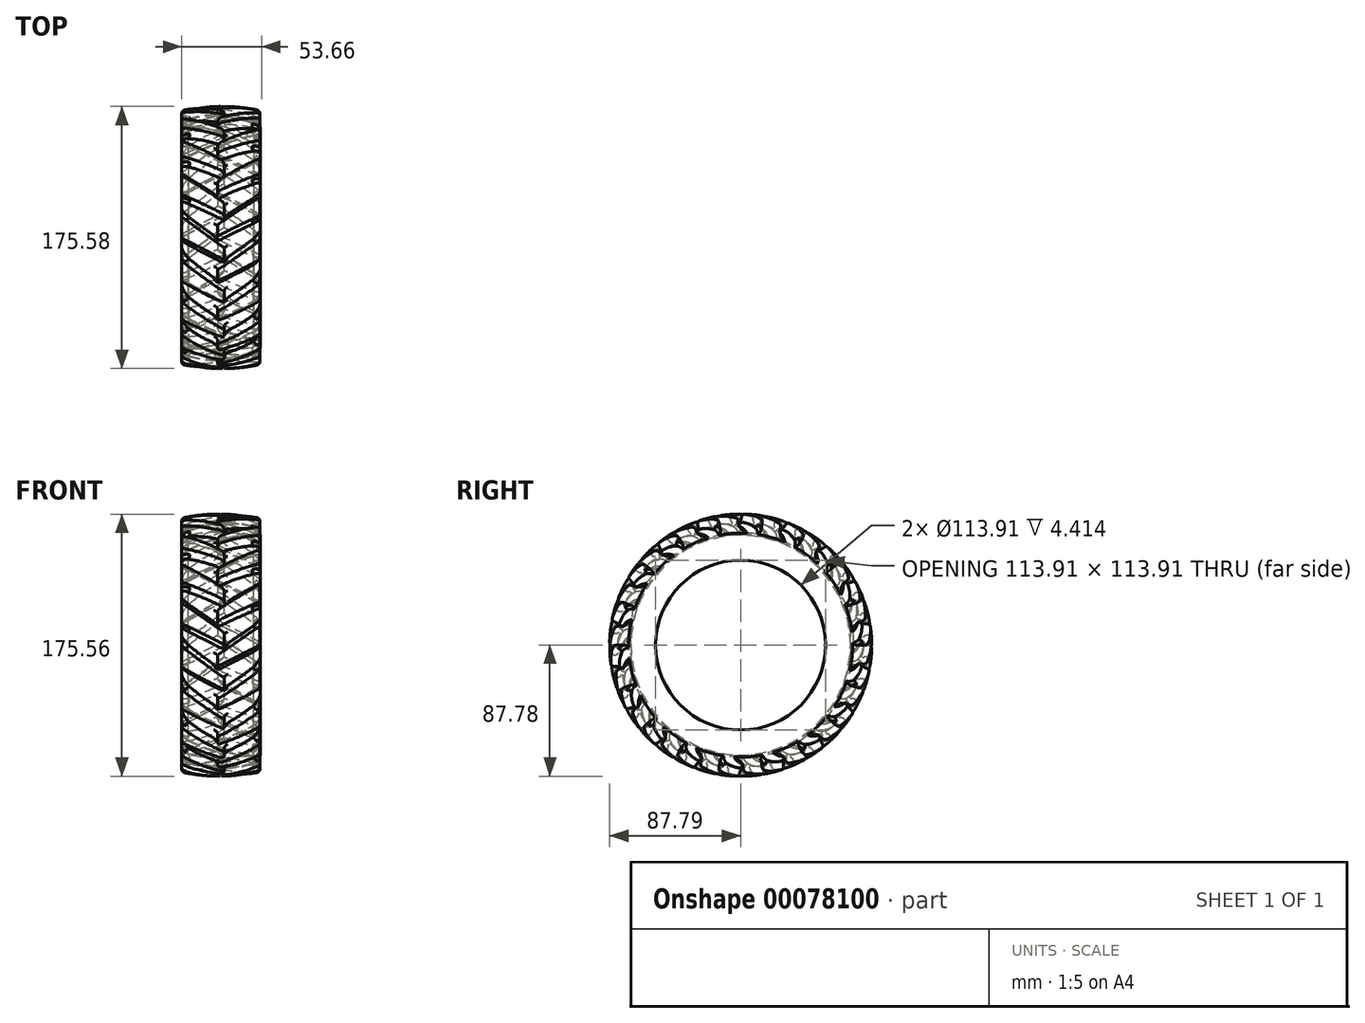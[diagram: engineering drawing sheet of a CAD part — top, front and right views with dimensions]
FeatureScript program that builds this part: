
annotation { "Feature Type Name" : "Feature", "Feature Type Description" : "" }
export const myFeature = defineFeature(function(context is Context, id is Id, definition is map)
    precondition{}
    {
        {
            var Q0;
            Q0=qCreatedBy(makeId("Top.planeOp"),FACE);
            var sketch = newSketch(context, id + "F0", { "sketchPlane" : qUnion([Q0])});
            skLineSegment(sketch, "E0", {"start": v(-41.36, 0) * mm, "end": v(39.08, 0) * mm});
            skLineSegment(sketch, "E1", {"start": v(0, 0) * mm, "end": v(0, 69.17) * mm});
            skLineSegment(sketch, "E2.bottom", {"start": v(26.28, 56.34) * mm, "end": v(-26.28, 56.34) * mm});
            skLineSegment(sketch, "E2.left", {"start": v(26.28, 56.34) * mm, "end": v(26.28, 73.43) * mm});
            skLineSegment(sketch, "E2.right", {"start": v(-26.28, 56.34) * mm, "end": v(-26.28, 73.43) * mm});
            skPoint(sketch, "E2.middle", {"position": v(0, 69.17) * mm});
            skArc(sketch, "E3", {"start": v(-21.6, 79.56) * mm, "mid": v(0, 82.44) * mm, "end": v(21.6, 79.56) * mm});
            skPoint(sketch, "E4.orphan", {"position": v(-26.28, 82) * mm});
            skPoint(sketch, "E5.orphan", {"position": v(26.28, 82) * mm});
            skPoint(sketch, "E6.visualSharp", {"position": v(-26.28, 78.14) * mm});
            skArc(sketch, "E6.filletArc", {"start": v(-21.6, 79.56) * mm, "mid": v(-24.97, 77.3) * mm, "end": v(-26.28, 73.43) * mm});
            skPoint(sketch, "E7.visualSharp", {"position": v(26.28, 78.14) * mm});
            skArc(sketch, "E7.filletArc", {"start": v(26.28, 73.43) * mm, "mid": v(24.97, 77.3) * mm, "end": v(21.6, 79.56) * mm});
            skSolve(sketch);
        }
        {
            var Q0;
            Q0 = qSketchRegion(id + "F0", true);
            var Q1;
            Q1=sQuery(id+"F0.wireOp",EDGE,"E0");
            revolve(context, id + "F1", {"entities" : qUnion([Q0]), "axis" : qUnion([Q1]), "revolveType" : RevolveType.FULL});
        }
        {
            var Q0;
            Q0=qCreatedBy(makeId("Top.planeOp"),FACE);
            var sketch = newSketch(context, id + "F2", { "sketchPlane" : qUnion([Q0])});
            skLineSegment(sketch, "E8", {"start": v(-26.25, 13.83) * mm, "end": v(2.16, -6.94) * mm});
            skLineSegment(sketch, "E9", {"start": v(2.16, -6.94) * mm, "end": v(2.16, -14.96) * mm});
            skLineSegment(sketch, "E10", {"start": v(2.16, -14.96) * mm, "end": v(-26.25, -0.3) * mm});
            skLineSegment(sketch, "E11", {"start": v(-26.25, 13.83) * mm, "end": v(-26.25, 0) * mm});
            skLineSegment(sketch, "E12", {"start": v(-26.25, 0) * mm, "end": v(-26.25, -0.3) * mm});
            skPoint(sketch, "E13.orphan", {"position": v(-26.83, 0) * mm});
            skLineSegment(sketch, "E14", {"start": v(-49.96, 0) * mm, "end": v(51.5, 0) * mm});
            skSolve(sketch);
        }
        {
            var Q0;
            Q0=makeQuery(id+"F2.imprint","IMPRINT",FACE,{"disambiguationData":[TD([[makeQuery(id+"F2.imprint","IMPRINT",EDGE,{"derivedFrom":sQuery(id+"F2.wireOp",EDGE,"E8")}),-1.0]])]});
            var Q1;
            {var subQ1=sQuery(id+"F2.wireOp",EDGE,"E9");Q1=makeQuery(id+"F2.imprint","IMPRINT",FACE,{"disambiguationData":[TD([[makeQuery(id+"F2.imprint","IMPRINT",EDGE,{"derivedFrom":subQ1}),-1.0]])]});}
            extrude(context, id + "F3", {"entities" : qUnion([Q0, Q1]), "operationType" : NewBodyOperationType.ADD, "depth" : 88.9 * mm});
        }
        {
            var Q0;
            Q0=qCreatedBy(makeId("Top.planeOp"),FACE);
            var Q1;
            Q1=sQuery(id+"F2.wireOp",EDGE,"E14");
            cPlane(context, id + "F4", {"entities" : qUnion([Q0, Q1]), "cplaneType" : CPlaneType.LINE_ANGLE, "offset" : 152.4 * mm, "angle" : 10 * degree, "width" : 152.4 * mm, "height" : 152.4 * mm});
        }
        {
            var Q0;
            Q0=qCreatedBy(id+"F4.planeOp",FACE);
            var sketch = newSketch(context, id + "F5", { "sketchPlane" : qUnion([Q0])});
            skLineSegment(sketch, "E15", {"start": v(-2.2, 14.33) * mm, "end": v(-2.2, 6.63) * mm});
            skLineSegment(sketch, "E16", {"start": v(-2.2, 6.63) * mm, "end": v(26.07, -12.68) * mm});
            skLineSegment(sketch, "E17", {"start": v(26.07, -12.68) * mm, "end": v(26.07, 0) * mm});
            skLineSegment(sketch, "E18", {"start": v(26.07, 0) * mm, "end": v(-2.2, 14.33) * mm});
            skSolve(sketch);
        }
        {
            var Q0;
            Q0=makeQuery(id+"F5.imprint","IMPRINT",FACE,{"disambiguationData":[TD([[makeQuery(id+"F5.imprint","IMPRINT",EDGE,{"derivedFrom":sQuery(id+"F5.wireOp",EDGE,"E15")}),1.0]])]});
            extrude(context, id + "F6", {"entities" : qUnion([Q0]), "operationType" : NewBodyOperationType.ADD, "oppositeDirection" : true, "depth" : 88.9 * mm});
        }
        {
            var Q0;
            Q0=qCreatedBy(makeId("Front.planeOp"),FACE);
            var sketch = newSketch(context, id + "F7", { "sketchPlane" : qUnion([Q0])});
            skArc(sketch, "E19", {"start": v(33.67, -83.2) * mm, "mid": v(-0.3, -87.8) * mm, "end": v(-34.27, -83.04) * mm});
            skLineSegment(sketch, "E20", {"start": v(-34.27, -83.04) * mm, "end": v(-34.27, -99.42) * mm});
            skLineSegment(sketch, "E21", {"start": v(-34.27, -99.42) * mm, "end": v(37.55, -99.42) * mm});
            skLineSegment(sketch, "E22", {"start": v(37.55, -99.42) * mm, "end": v(33.67, -83.2) * mm});
            skArc(sketch, "E23", {"start": v(21.86, -73.58) * mm, "mid": v(0, -75.71) * mm, "end": v(-21.86, -73.58) * mm});
            skLineSegment(sketch, "E24", {"start": v(-21.86, -73.58) * mm, "end": v(-21.86, -56.95) * mm});
            skLineSegment(sketch, "E25", {"start": v(-21.86, 0) * mm, "end": v(21.86, 0) * mm});
            skLineSegment(sketch, "E26", {"start": v(21.86, -56.95) * mm, "end": v(21.86, -73.58) * mm});
            skLineSegment(sketch, "E27", {"start": v(21.86, -56.95) * mm, "end": v(33.74, -56.95) * mm});
            skLineSegment(sketch, "E28", {"start": v(33.74, -56.95) * mm, "end": v(33.74, 0) * mm});
            skLineSegment(sketch, "E29", {"start": v(33.74, 0) * mm, "end": v(21.86, 0) * mm});
            skLineSegment(sketch, "E30", {"start": v(0, 0) * mm, "end": v(0, -57.21) * mm});
            skPoint(sketch, "E30.endSnap0", {"position": v(0, 0) * mm});
            skLineSegment(sketch, "E31.MirrorCS", {"start": v(-21.86, -56.95) * mm, "end": v(-33.74, -56.95) * mm});
            skLineSegment(sketch, "E32.MirrorCS", {"start": v(-33.74, -56.95) * mm, "end": v(-33.74, 0) * mm});
            skLineSegment(sketch, "E33.MirrorCS", {"start": v(-33.74, 0) * mm, "end": v(-21.86, 0) * mm});
            skSolve(sketch);
        }
        {
            var Q0;
            Q0 = qSketchRegion(id + "F7", true);
            var Q1;
            Q1=sQuery(id+"F2.wireOp",EDGE,"E14");
            revolve(context, id + "F8", {"operationType" : NewBodyOperationType.REMOVE, "entities" : qUnion([Q0]), "axis" : qUnion([Q1]), "revolveType" : RevolveType.FULL, "oppositeDirection" : true});
        }
        {
            var Q0;
            Q0=makeQuery(id+"F6.boolean.opBoolean","INTERSECT",EDGE,{"derivedFrom":[makeQuery(id+"F1.opRevolve","SWEPT_FACE",FACE,{"disambiguationData":[OSD([sQuery(id+"F0.wireOp",EDGE,"E3")])]}),makeQuery(id+"F6.opExtrude","SWEPT_FACE",FACE,{"disambiguationData":[OSD([sQuery(id+"F5.wireOp",EDGE,"E18")])]})]});
            var Q1;
            Q1=makeQuery(id+"F6.boolean.opBoolean","INTERSECT",EDGE,{"derivedFrom":[makeQuery(id+"F1.opRevolve","SWEPT_FACE",FACE,{"disambiguationData":[OSD([sQuery(id+"F0.wireOp",EDGE,"E3")])]}),makeQuery(id+"F6.opExtrude","SWEPT_FACE",FACE,{"disambiguationData":[OSD([sQuery(id+"F5.wireOp",EDGE,"E16")])]})]});
            var Q2;
            Q2=makeQuery(id+"F3.boolean.opBoolean","INTERSECT",EDGE,{"derivedFrom":[makeQuery(id+"F1.opRevolve","SWEPT_FACE",FACE,{"disambiguationData":[OSD([sQuery(id+"F0.wireOp",EDGE,"E3")])]}),makeQuery(id+"F3.opExtrude","SWEPT_FACE",FACE,{"disambiguationData":[OSD([sQuery(id+"F2.wireOp",EDGE,"E8")])]})]});
            var Q3;
            Q3=makeQuery(id+"F3.boolean.opBoolean","INTERSECT",EDGE,{"derivedFrom":[makeQuery(id+"F1.opRevolve","SWEPT_FACE",FACE,{"disambiguationData":[OSD([sQuery(id+"F0.wireOp",EDGE,"E3")])]}),makeQuery(id+"F3.opExtrude","SWEPT_FACE",FACE,{"disambiguationData":[OSD([sQuery(id+"F2.wireOp",EDGE,"E10")])]})]});
            var Q4;
            Q4=makeQuery(id+"F6.boolean.opBoolean","INTERSECT",EDGE,{"derivedFrom":[makeQuery(id+"F1.opRevolve","SWEPT_FACE",FACE,{"disambiguationData":[OSD([sQuery(id+"F0.wireOp",EDGE,"E3")])]}),makeQuery(id+"F6.opExtrude","SWEPT_FACE",FACE,{"disambiguationData":[OSD([sQuery(id+"F5.wireOp",EDGE,"E15")])]})]});
            var Q5;
            Q5=makeQuery(id+"F3.boolean.opBoolean","INTERSECT",EDGE,{"derivedFrom":[makeQuery(id+"F1.opRevolve","SWEPT_FACE",FACE,{"disambiguationData":[OSD([sQuery(id+"F0.wireOp",EDGE,"E3")])]}),makeQuery(id+"F3.opExtrude","SWEPT_FACE",FACE,{"disambiguationData":[OSD([sQuery(id+"F2.wireOp",EDGE,"E9")])]})]});
            var Q6;
            {var subQ2=sQuery(id+"F2.wireOp",EDGE,"E12");var subQ3=sQuery(id+"F2.wireOp",EDGE,"E11");Q6=makeQuery(id+"F8.boolean.opBoolean","INTERSECT",EDGE,{"derivedFrom":[makeQuery(id+"F3.boolean.opBoolean","SPLIT",FACE,{"disambiguationData":[TD([makeQuery(id+"F1.opRevolve","SWEPT_FACE",FACE,{"disambiguationData":[OSD([sQuery(id+"F0.wireOp",EDGE,"E6.filletArc")])]})])],"derivedFrom":makeQuery(id+"F3.opExtrude","SWEPT_FACE",FACE,{"disambiguationData":[OSD([subQ3,subQ2])]})}),makeQuery(id+"F8.opRevolve","SWEPT_FACE",FACE,{"disambiguationData":[OSD([sQuery(id+"F7.wireOp",EDGE,"E19")])]})]});}
            var Q7;
            {var subQ2=sQuery(id+"F2.wireOp",EDGE,"E9");Q7=makeQuery(id+"F8.boolean.opBoolean","INTERSECT",EDGE,{"derivedFrom":[makeQuery(id+"F3.boolean.opBoolean","SPLIT",FACE,{"disambiguationData":[TD([makeQuery(id+"F1.opRevolve","SWEPT_FACE",FACE,{"disambiguationData":[OSD([sQuery(id+"F0.wireOp",EDGE,"E3")])]})])],"derivedFrom":makeQuery(id+"F3.opExtrude","SWEPT_FACE",FACE,{"disambiguationData":[OSD([subQ2])]})}),makeQuery(id+"F8.opRevolve","SWEPT_FACE",FACE,{"disambiguationData":[OSD([sQuery(id+"F7.wireOp",EDGE,"E19")])]})]});}
            var Q8;
            {var subQ2=sQuery(id+"F5.wireOp",EDGE,"E15");Q8=makeQuery(id+"F8.boolean.opBoolean","INTERSECT",EDGE,{"derivedFrom":[makeQuery(id+"F6.boolean.opBoolean","SPLIT",FACE,{"disambiguationData":[TD([makeQuery(id+"F1.opRevolve","SWEPT_FACE",FACE,{"disambiguationData":[OSD([sQuery(id+"F0.wireOp",EDGE,"E3")])]})])],"derivedFrom":makeQuery(id+"F6.opExtrude","SWEPT_FACE",FACE,{"disambiguationData":[OSD([subQ2])]})}),makeQuery(id+"F8.opRevolve","SWEPT_FACE",FACE,{"disambiguationData":[OSD([sQuery(id+"F7.wireOp",EDGE,"E19")])]})]});}
            var Q9;
            {var subQ2=sQuery(id+"F5.wireOp",EDGE,"E17");Q9=makeQuery(id+"F8.boolean.opBoolean","INTERSECT",EDGE,{"derivedFrom":[makeQuery(id+"F6.boolean.opBoolean","SPLIT",FACE,{"disambiguationData":[TD([makeQuery(id+"F1.opRevolve","SWEPT_FACE",FACE,{"disambiguationData":[OSD([sQuery(id+"F0.wireOp",EDGE,"E7.filletArc")])]})])],"derivedFrom":makeQuery(id+"F6.opExtrude","SWEPT_FACE",FACE,{"disambiguationData":[OSD([subQ2])]})}),makeQuery(id+"F8.opRevolve","SWEPT_FACE",FACE,{"disambiguationData":[OSD([sQuery(id+"F7.wireOp",EDGE,"E19")])]})]});}
            fillet(context, id + "F9", {"entities" : qUnion([Q0, Q1, Q2, Q3, Q4, Q5, Q6, Q7, Q8, Q9]), "radius" : 2.54 * mm, "tangentPropagation" : true, "allowEdgeOverflow" : false});
        }
        {
            var Q0;
            Q0=makeQuery(id+"F1.opRevolve","SWEPT_BODY",BODY,{"disambiguationData":[OSD([sQuery(id+"F0.wireOp",EDGE,"E2.bottom"),sQuery(id+"F0.wireOp",EDGE,"E2.left"),sQuery(id+"F0.wireOp",EDGE,"E2.right"),sQuery(id+"F0.wireOp",EDGE,"E3"),sQuery(id+"F0.wireOp",EDGE,"E6.filletArc"),sQuery(id+"F0.wireOp",EDGE,"E7.filletArc")])]});
            var Q1;
            Q1=sQuery(id+"F2.wireOp",EDGE,"E14");
            circularPattern(context, id + "F10", {"operationType" : NewBodyOperationType.ADD, "entities" : qUnion([Q0]), "axis" : qUnion([Q1]), "angle" : 20 * degree, "instanceCount" : 18});
        }
    });
